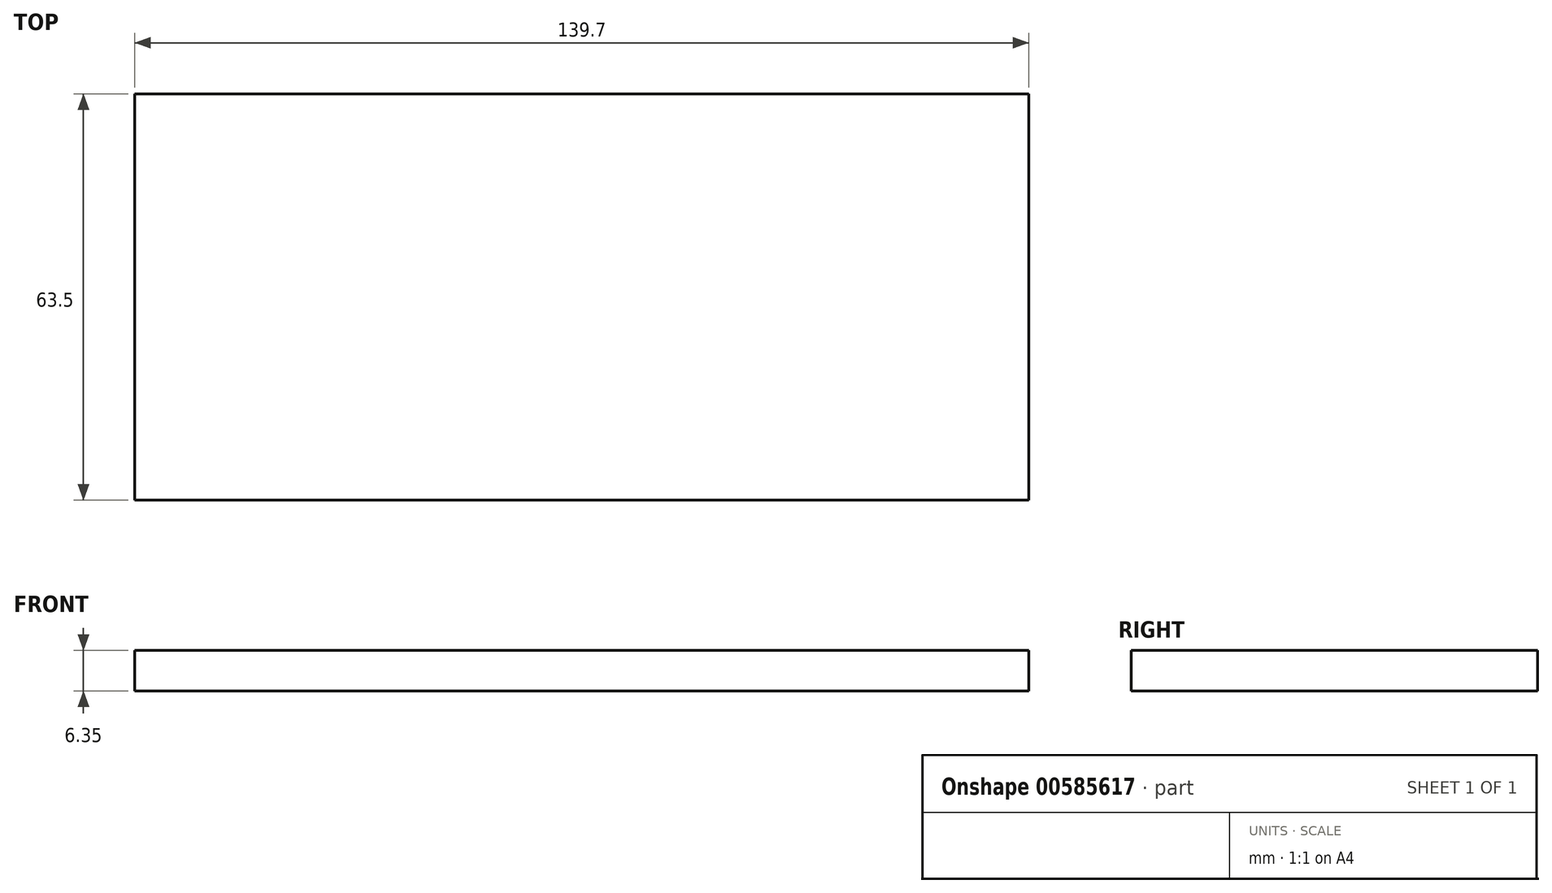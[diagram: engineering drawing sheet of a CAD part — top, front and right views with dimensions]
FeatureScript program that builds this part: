
annotation { "Feature Type Name" : "Feature", "Feature Type Description" : "" }
export const myFeature = defineFeature(function(context is Context, id is Id, definition is map)
    precondition{}
    {
        {
            var Q0;
            Q0=qCreatedBy(makeId("Top.planeOp"),FACE);
            var sketch = newSketch(context, id + "F0", { "sketchPlane" : qUnion([Q0])});
            skLineSegment(sketch, "E0.bottom", {"start": v(-69.85, 31.75) * mm, "end": v(69.85, 31.75) * mm});
            skLineSegment(sketch, "E0.top", {"start": v(-69.85, -31.75) * mm, "end": v(69.85, -31.75) * mm});
            skLineSegment(sketch, "E0.left", {"start": v(-69.85, 31.75) * mm, "end": v(-69.85, -31.75) * mm});
            skLineSegment(sketch, "E0.right", {"start": v(69.85, 31.75) * mm, "end": v(69.85, -31.75) * mm});
            skPoint(sketch, "E0.middle", {"position": v(0, 0) * mm});
            skSolve(sketch);
        }
        {
            var Q0;
            Q0=makeQuery(id+"F0.imprint","IMPRINT",FACE,{"disambiguationData":[TD([[makeQuery(id+"F0.imprint","IMPRINT",EDGE,{"derivedFrom":sQuery(id+"F0.wireOp",EDGE,"E0.bottom")}),-1.0]])]});
            extrude(context, id + "F1", {"entities" : qUnion([Q0]), "depth" : 6.35 * mm, "offsetDistance" : 25.4 * mm});
        }
    });
